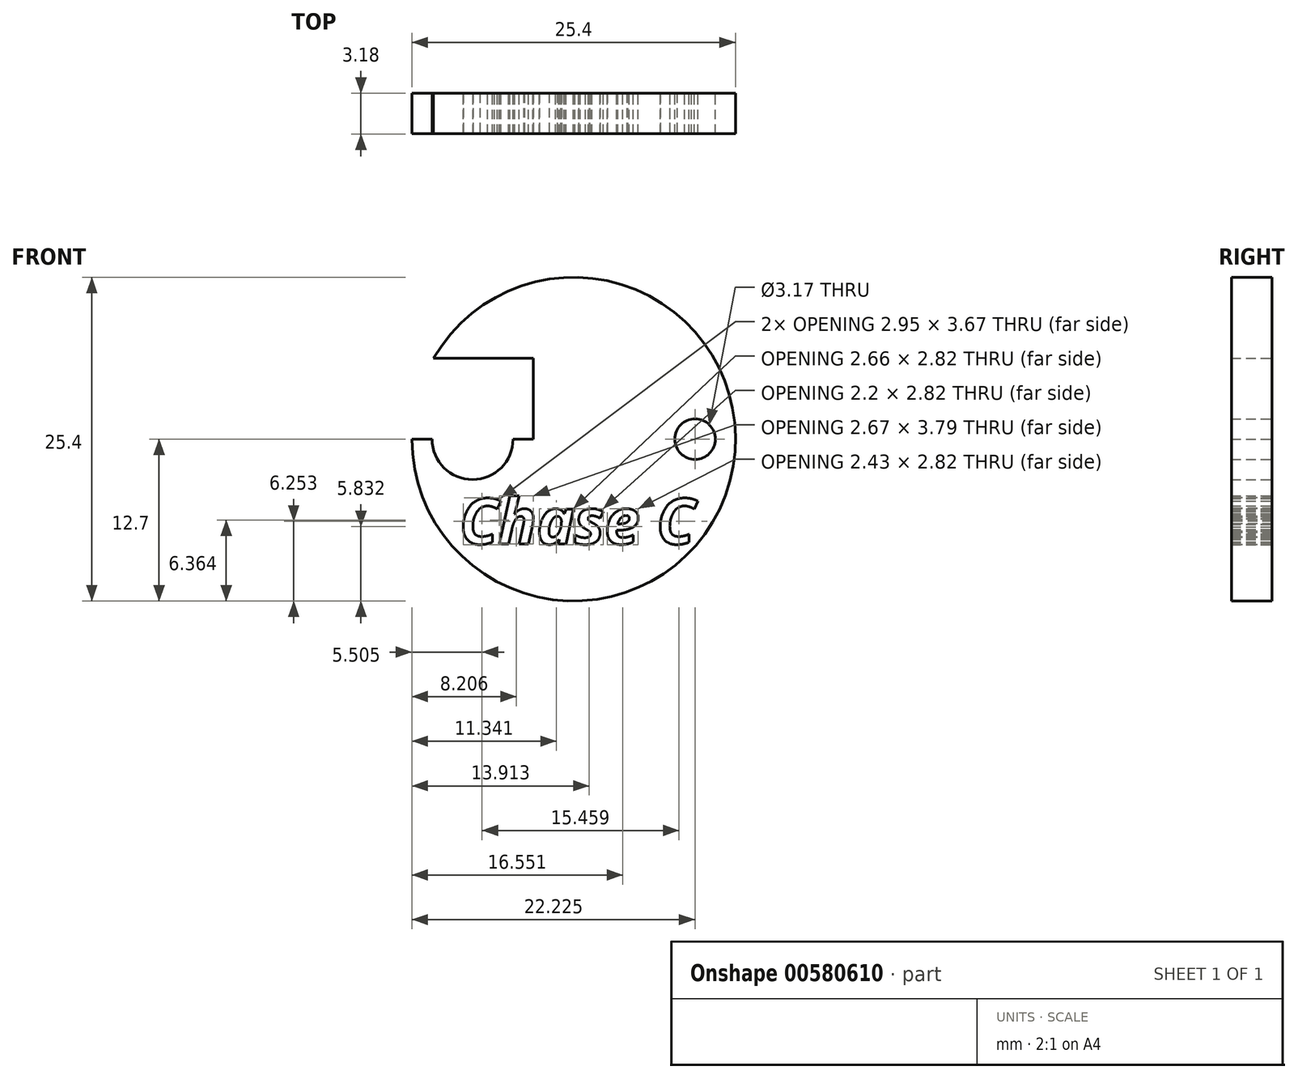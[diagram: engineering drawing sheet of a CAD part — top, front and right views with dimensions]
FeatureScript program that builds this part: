
annotation { "Feature Type Name" : "Feature", "Feature Type Description" : "" }
export const myFeature = defineFeature(function(context is Context, id is Id, definition is map)
    precondition{}
    {
        {
            var Q0;
            Q0=qCreatedBy(makeId("Front.planeOp"),FACE);
            var sketch = newSketch(context, id + "F0", { "sketchPlane" : qUnion([Q0])});
            skArc(sketch, "E0", {"start": v(-12.7, 0) * mm, "mid": v(12.27, -3.29) * mm, "end": v(-11, 6.35) * mm});
            skLineSegment(sketch, "E1.bottom", {"start": v(-11, 6.35) * mm, "end": v(-3.18, 6.35) * mm});
            skLineSegment(sketch, "E1.top", {"start": v(-12.7, 0) * mm, "end": v(-11.11, 0) * mm});
            skLineSegment(sketch, "E1.right", {"start": v(-3.18, 6.35) * mm, "end": v(-3.18, 0) * mm});
            skArc(sketch, "E2", {"start": v(-11.11, 0) * mm, "mid": v(-7.94, -3.18) * mm, "end": v(-4.76, 0) * mm});
            skPoint(sketch, "E2.first.point", {"position": v(-10.95, -1) * mm});
            skPoint(sketch, "E2.second.point", {"position": v(-7.88, -3.17) * mm});
            skPoint(sketch, "E2.third.point", {"position": v(-8, -3.17) * mm});
            skLineSegment(sketch, "E3.trimOffspring", {"start": v(-4.76, 0) * mm, "end": v(-3.18, 0) * mm});
            skSolve(sketch);
        }
        {
            var Q0;
            Q0 = qSketchRegion(id + "F0", true);
            extrude(context, id + "F1", {"entities" : qUnion([Q0]), "depth" : 3.17 * mm, "offsetDistance" : 25.4 * mm});
        }
        {
            var Q0;
            Q0=qCreatedBy(makeId("Front.planeOp"),FACE);
            var sketch = newSketch(context, id + "F2", { "sketchPlane" : qUnion([Q0])});
            skCircle(sketch, "E4", {"center": v(9.53, 0) * mm, "radius": 1.59 * mm});
            skPoint(sketch, "E4.first.point", {"position": v(8.39, 1.1) * mm});
            skPoint(sketch, "E4.second.point", {"position": v(10.82, -0.93) * mm});
            skPoint(sketch, "E4.third.point", {"position": v(10.85, 0.87) * mm});
            skSolve(sketch);
        }
        {
            var Q0;
            Q0 = qSketchRegion(id + "F2", true);
            extrude(context, id + "F3", {"entities" : qUnion([Q0]), "operationType" : NewBodyOperationType.REMOVE, "endBound" : BoundingType.THROUGH_ALL, "depth" : 3.17 * mm, "offsetDistance" : 25.4 * mm});
        }
        {
            var Q0;
            Q0=qCreatedBy(makeId("Front.planeOp"),FACE);
            var sketch = newSketch(context, id + "F4", { "sketchPlane" : qUnion([Q0])});
            skText(sketch, "E5", { "text": "Chase C", "fontName": "OpenSans-BoldItalic.ttf"});
            const initialGuessF4  = {"E5": [-0.00897, -0.00823, 1, 0, 0.00359]};
            skSetInitialGuess(sketch, initialGuessF4);
            skSolve(sketch);
        }
        {
            var Q0;
            Q0 = qSketchRegion(id + "F4", true);
            extrude(context, id + "F5", {"entities" : qUnion([Q0]), "operationType" : NewBodyOperationType.REMOVE, "endBound" : BoundingType.THROUGH_ALL, "depth" : 25.4 * mm, "offsetDistance" : 25.4 * mm});
        }
    });
